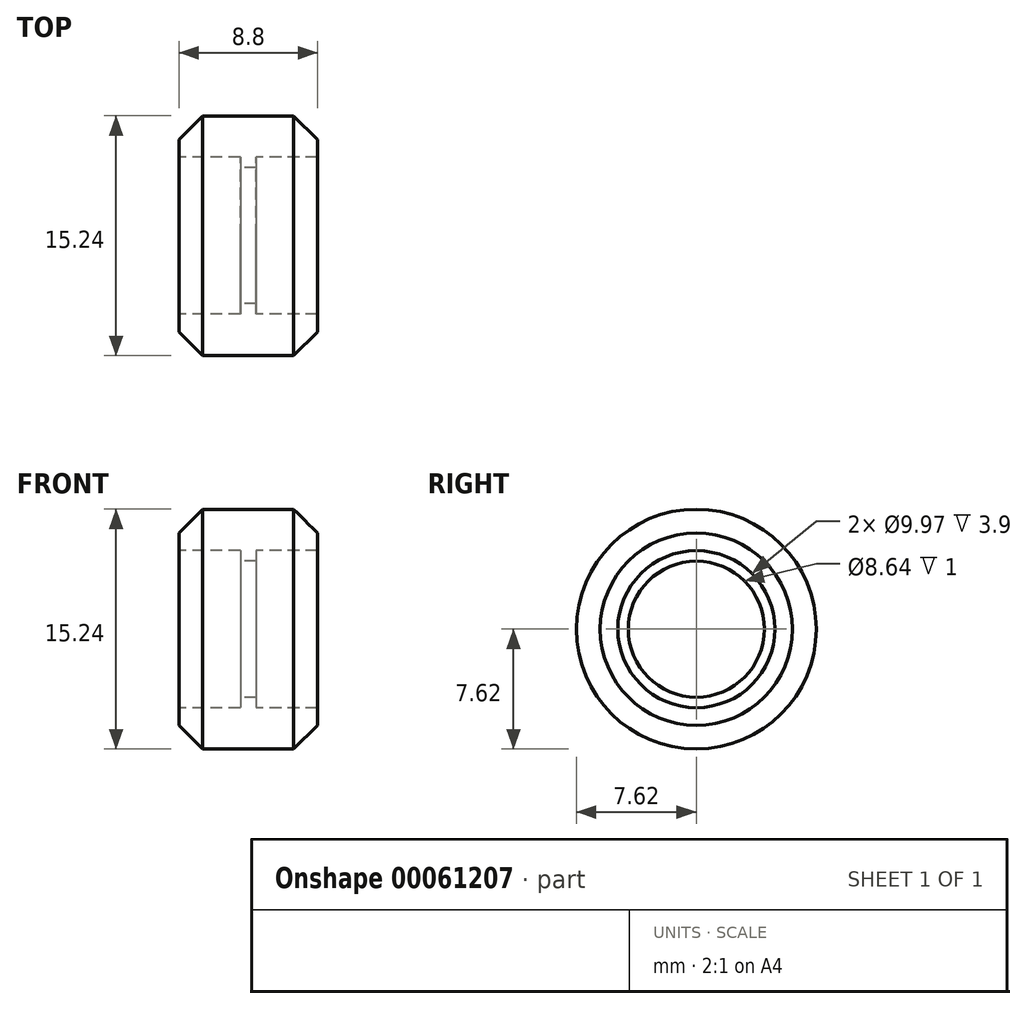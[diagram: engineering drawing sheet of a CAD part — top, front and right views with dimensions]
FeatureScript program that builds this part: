
annotation { "Feature Type Name" : "Feature", "Feature Type Description" : "" }
export const myFeature = defineFeature(function(context is Context, id is Id, definition is map)
    precondition{}
    {
        {
            var Q0;
            Q0=qCreatedBy(makeId("Front.planeOp"),FACE);
            var sketch = newSketch(context, id + "F0", { "sketchPlane" : qUnion([Q0])});
            skLineSegment(sketch, "E0", {"start": v(2.9, 7.62) * mm, "end": v(-2.89, 7.62) * mm});
            skLineSegment(sketch, "E1", {"start": v(4.4, 4.99) * mm, "end": v(-4.4, 4.99) * mm, "construction": true});
            skLineSegment(sketch, "E2", {"start": v(4.4, 4.99) * mm, "end": v(4.4, 6.1) * mm});
            skLineSegment(sketch, "E3", {"start": v(-4.4, 4.99) * mm, "end": v(-4.4, 6.1) * mm});
            skLineSegment(sketch, "E4", {"start": v(-4.4, 6.1) * mm, "end": v(4.4, 6.1) * mm, "construction": true});
            skLineSegment(sketch, "E5", {"start": v(0.5, 4.99) * mm, "end": v(0.5, 4.32) * mm});
            skLineSegment(sketch, "E6", {"start": v(0.5, 4.32) * mm, "end": v(-0.5, 4.32) * mm});
            skLineSegment(sketch, "E7", {"start": v(-0.5, 4.32) * mm, "end": v(-0.5, 4.99) * mm});
            skLineSegment(sketch, "E8", {"start": v(0.5, 4.99) * mm, "end": v(4.4, 4.99) * mm});
            skLineSegment(sketch, "E9", {"start": v(-0.5, 4.99) * mm, "end": v(-4.4, 4.99) * mm});
            skLineSegment(sketch, "E10", {"start": v(-2.89, 7.62) * mm, "end": v(-4.4, 6.1) * mm});
            skLineSegment(sketch, "E11", {"start": v(2.89, 7.62) * mm, "end": v(4.4, 6.1) * mm});
            skLineSegment(sketch, "E12", {"start": v(-7.51, 0) * mm, "end": v(9.66, 0) * mm});
            skSolve(sketch);
        }
        {
            var Q0;
            Q0=makeQuery(id+"F0.imprint","IMPRINT",FACE,{"disambiguationData":[TD([[makeQuery(id+"F0.imprint","IMPRINT",EDGE,{"derivedFrom":sQuery(id+"F0.wireOp",EDGE,"E0")}),1.0]])]});
            var Q1;
            Q1=sQuery(id+"F0.wireOp",EDGE,"E12");
            revolve(context, id + "F1", {"entities" : qUnion([Q0]), "axis" : qUnion([Q1]), "revolveType" : RevolveType.FULL});
        }
    });
